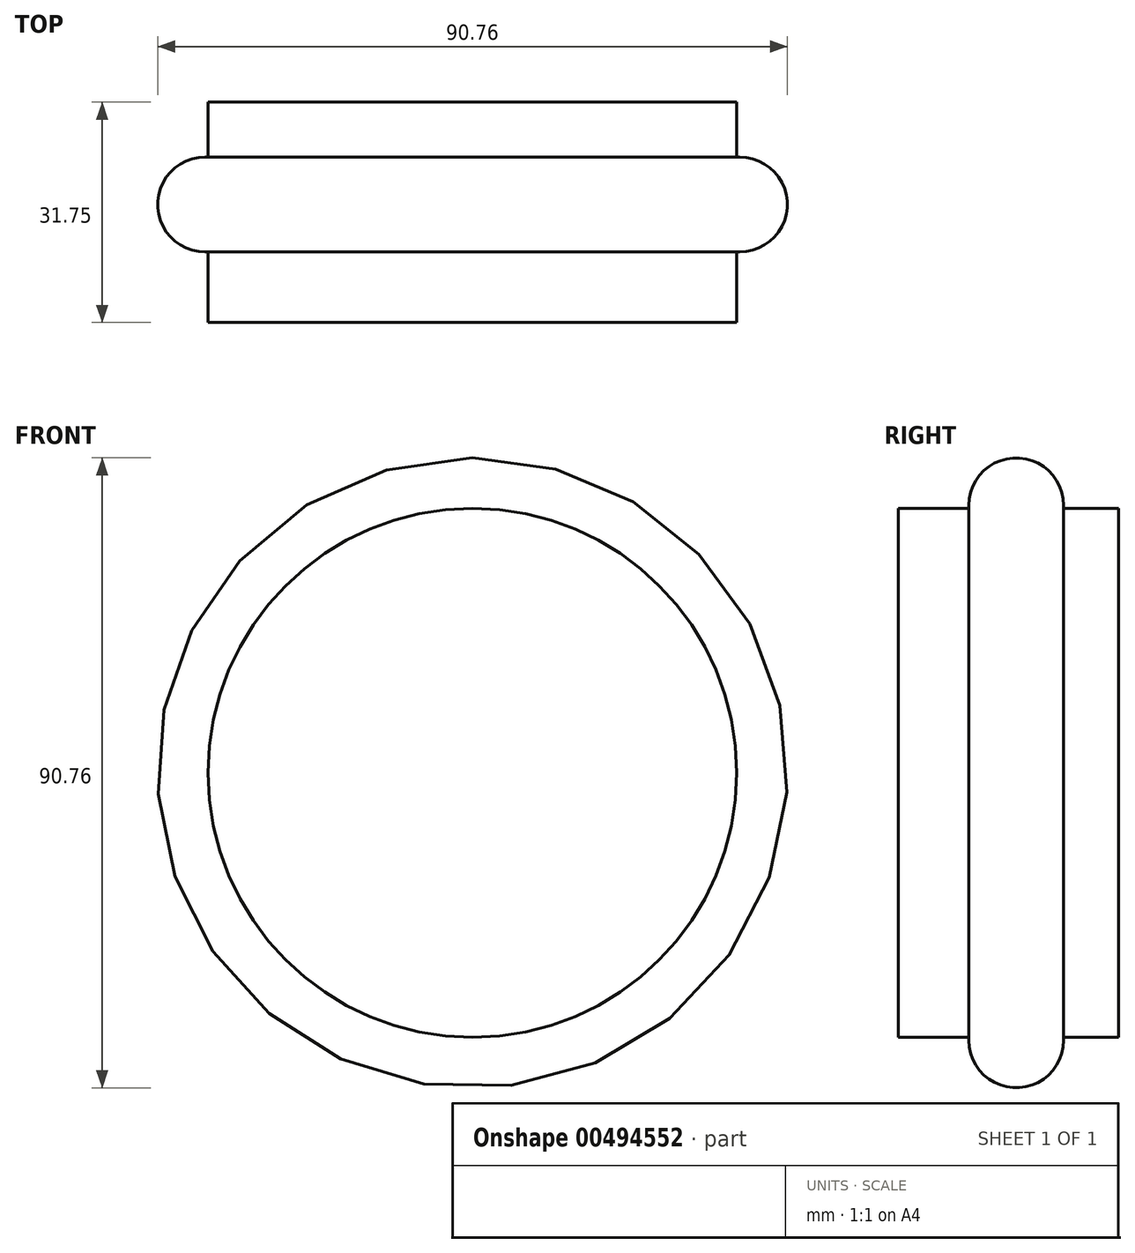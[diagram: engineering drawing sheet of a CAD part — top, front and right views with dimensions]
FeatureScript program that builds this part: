
annotation { "Feature Type Name" : "Feature", "Feature Type Description" : "" }
export const myFeature = defineFeature(function(context is Context, id is Id, definition is map)
    precondition{}
    {
        {
            var Q0;
            Q0=qCreatedBy(makeId("Front.planeOp"),FACE);
            var sketch = newSketch(context, id + "F0", { "sketchPlane" : qUnion([Q0])});
            skCircle(sketch, "E0", {"center": v(0, 0) * mm, "radius": 38.1 * mm});
            skSolve(sketch);
        }
        {
            var Q0;
            Q0=makeQuery(id+"F0.imprint","IMPRINT",FACE,{"disambiguationData":[TD([[makeQuery(id+"F0.imprint","IMPRINT",EDGE,{"derivedFrom":sQuery(id+"F0.wireOp",EDGE,"E0")}),1.0]])]});
            extrude(context, id + "F1", {"entities" : qUnion([Q0]), "depth" : 31.75 * mm});
        }
        {
            var Q0;
            Q0=qCreatedBy(makeId("Top.planeOp"),FACE);
            var sketch = newSketch(context, id + "F2", { "sketchPlane" : qUnion([Q0])});
            skCircle(sketch, "E1", {"center": v(38.55, -14.75) * mm, "radius": 6.83 * mm});
            skSolve(sketch);
        }
        {
            var Q0;
            Q0=makeQuery(id+"F2.imprint","IMPRINT",FACE,{"disambiguationData":[TD([[makeQuery(id+"F2.imprint","IMPRINT",EDGE,{"derivedFrom":sQuery(id+"F2.wireOp",EDGE,"E1")}),1.0]])]});
            var Q1;
            Q1=makeQuery(id+"F1.opExtrude","CAP_EDGE",EDGE,{"disambiguationData":[OSD([sQuery(id+"F0.wireOp",EDGE,"E0")])],"isStart":false});
            revolve(context, id + "F3", {"operationType" : NewBodyOperationType.ADD, "entities" : qUnion([Q0]), "axis" : qUnion([Q1]), "revolveType" : RevolveType.FULL});
        }
    });
